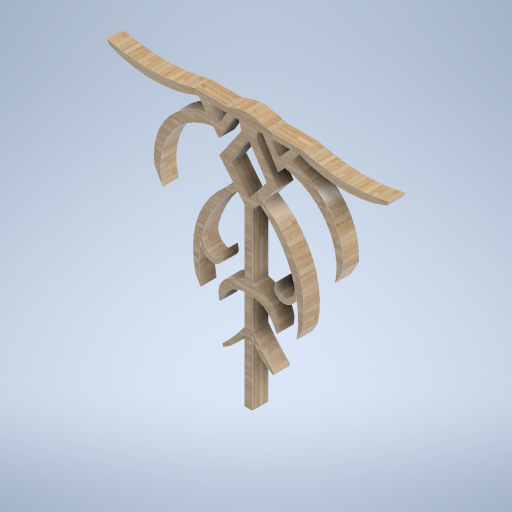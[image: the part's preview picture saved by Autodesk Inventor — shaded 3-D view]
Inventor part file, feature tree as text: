
AUTODESK INVENTOR PART (.ipt)
format: ipt  version: 2024.2 (Build 282272000, 272)  size: 593,920 bytes
history: native  units: mm
features: sketch x4, extrude x3, projected_geometry x2, plane x1
ambient origin geometry x8: Origin, YZ Plane, XZ Plane, XY Plane, X Axis, Y Axis, Z Axis, Center Point
bodies: Solid1 (feature_tree)
feature tree (10):
  extrude  "Extrusion1"  Depth=200.0mm TaperAngle=0.0deg
  extrude  "Extrusion2"  Depth=600.0mm
  extrude  "Extrusion3"  Depth=500.0mm
  plane  "Work Plane1"
  sketch  "Sketch4"  dims[d11=24.43461mm d12=0.0mm d13=0.0mm d14=200.0mm d15=0.0mm d16=-100.0mm]
  sketch  "Sketch1"  dims[d0=180.0deg d1=200.0mm d2=0.0mm]
  sketch  "Sketch2"  dims[d4=800.0mm d7=600.0mm]
  projected_geometry  "Projected Loop1"
  sketch  "Sketch3"  dims[d9=1400.0mm d10=500.0mm]
  projected_geometry  "Projected Loop2"
